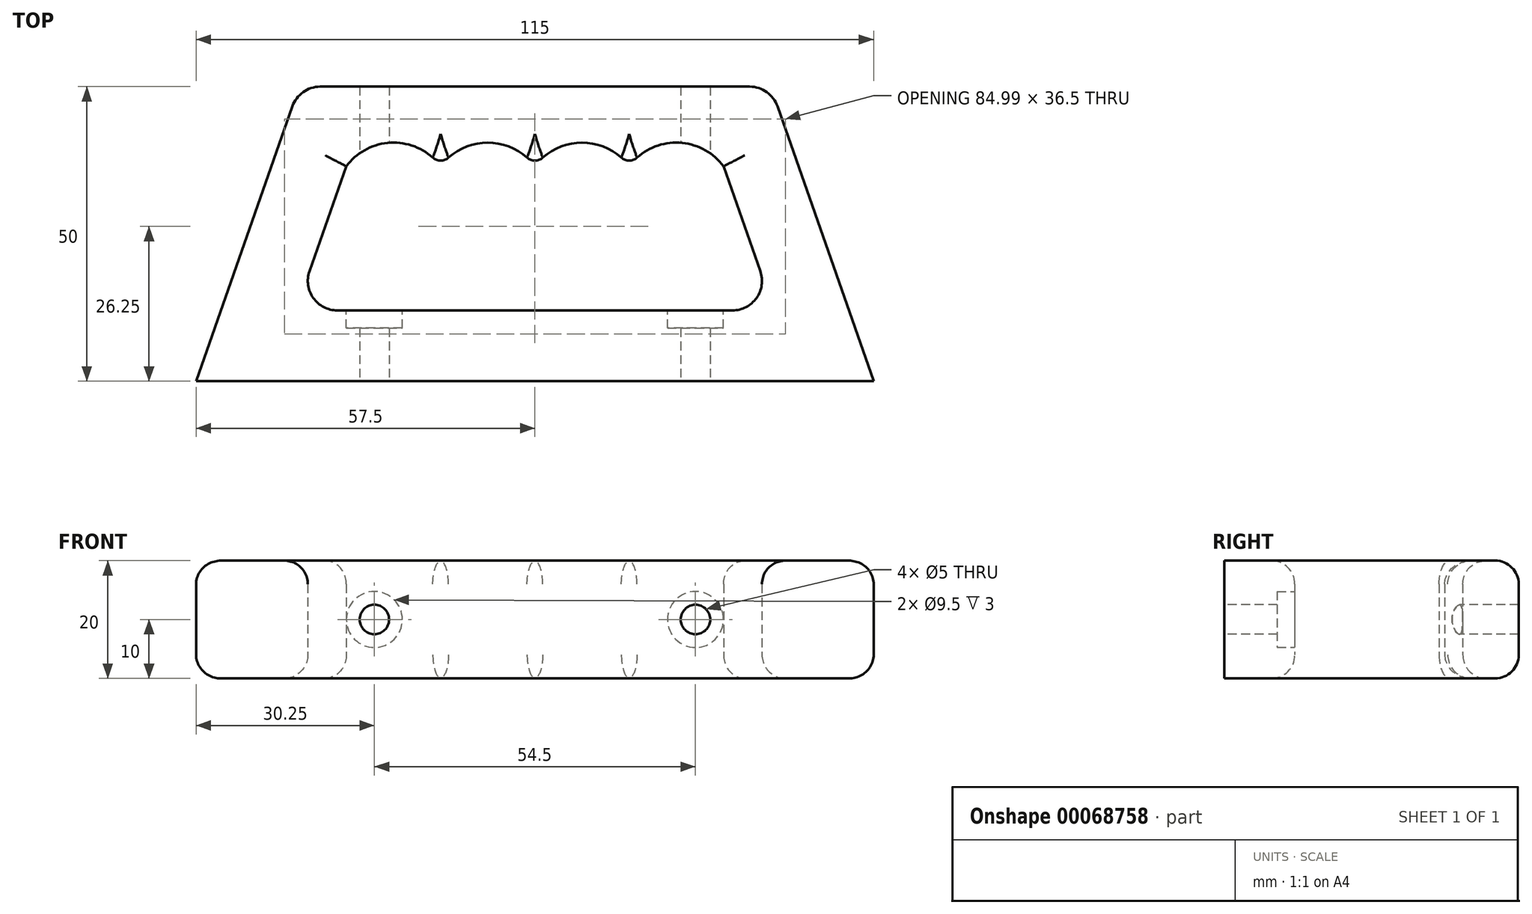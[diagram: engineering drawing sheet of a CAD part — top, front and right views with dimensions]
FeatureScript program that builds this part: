
annotation { "Feature Type Name" : "Feature", "Feature Type Description" : "" }
export const myFeature = defineFeature(function(context is Context, id is Id, definition is map)
    precondition{}
    {
        {
            var Q0;
            Q0=qCreatedBy(makeId("Top.planeOp"),FACE);
            var sketch = newSketch(context, id + "F0", { "sketchPlane" : qUnion([Q0])});
            skLineSegment(sketch, "E0.rect.bottom", {"start": v(57.5, 25) * mm, "end": v(-57.5, 25) * mm, "construction": true});
            skLineSegment(sketch, "E0.rect.top", {"start": v(57.5, -25) * mm, "end": v(-57.5, -25) * mm, "construction": true});
            skLineSegment(sketch, "E0.rect.left", {"start": v(57.5, 25) * mm, "end": v(57.5, -25) * mm, "construction": true});
            skLineSegment(sketch, "E0.rect.right", {"start": v(-57.5, 25) * mm, "end": v(-57.5, -25) * mm, "construction": true});
            skPoint(sketch, "E0.rect.middle", {"position": v(0, 0) * mm});
            skLineSegment(sketch, "E1", {"start": v(-57.5, -25) * mm, "end": v(57.5, -25) * mm});
            skLineSegment(sketch, "E2", {"start": v(57.5, -25) * mm, "end": v(41.17, 21.65) * mm});
            skLineSegment(sketch, "E3", {"start": v(36.45, 25) * mm, "end": v(-36.45, 25) * mm});
            skLineSegment(sketch, "E4", {"start": v(-41.17, 21.65) * mm, "end": v(-57.5, -25) * mm});
            skLineSegment(sketch, "E5.rect.bottom", {"start": v(24, 5.5) * mm, "end": v(-24, 5.5) * mm, "construction": true});
            skLineSegment(sketch, "E5.rect.top", {"start": v(24, -5.5) * mm, "end": v(-24, -5.5) * mm, "construction": true});
            skLineSegment(sketch, "E5.rect.left", {"start": v(24, 5.5) * mm, "end": v(24, -5.5) * mm, "construction": true});
            skLineSegment(sketch, "E5.rect.right", {"start": v(-24, 5.5) * mm, "end": v(-24, -5.5) * mm, "construction": true});
            skPoint(sketch, "E6.visualSharp", {"position": v(-40, 25) * mm});
            skArc(sketch, "E6.filletArc", {"start": v(-36.45, 25) * mm, "mid": v(-39.35, 24.08) * mm, "end": v(-41.17, 21.65) * mm});
            skPoint(sketch, "E7.visualSharp", {"position": v(40, 25) * mm});
            skArc(sketch, "E7.filletArc", {"start": v(41.17, 21.65) * mm, "mid": v(39.35, 24.08) * mm, "end": v(36.45, 25) * mm});
            skLineSegment(sketch, "E8.0", {"start": v(-32.02, 11.47) * mm, "end": v(-38.26, -6.35) * mm});
            skLineSegment(sketch, "E8.2", {"start": v(38.26, -6.35) * mm, "end": v(32.02, 11.47) * mm});
            skLineSegment(sketch, "E8.3", {"start": v(-33.54, -13) * mm, "end": v(33.54, -13) * mm});
            skArc(sketch, "E9", {"start": v(-16, 11.5) * mm, "mid": v(-24.02, 15.5) * mm, "end": v(-32.02, 11.47) * mm});
            skArc(sketch, "E10.1.0.0", {"start": v(0, 11.5) * mm, "mid": v(-8, 15.5) * mm, "end": v(-16, 11.5) * mm});
            skArc(sketch, "E10.2.0.0", {"start": v(16, 11.5) * mm, "mid": v(8, 15.5) * mm, "end": v(0, 11.5) * mm});
            skArc(sketch, "E10.3.0.0", {"start": v(32.02, 11.47) * mm, "mid": v(24.02, 15.5) * mm, "end": v(16, 11.5) * mm});
            skLineSegment(sketch, "E10.direction1", {"start": v(-24, 5.5) * mm, "end": v(-8, 5.5) * mm, "construction": true});
            skPoint(sketch, "E11.orphan", {"position": v(31.49, 13) * mm});
            skPoint(sketch, "E12.visualSharp", {"position": v(-40.59, -13) * mm});
            skArc(sketch, "E12.filletArc", {"start": v(-38.26, -6.35) * mm, "mid": v(-37.62, -10.9) * mm, "end": v(-33.54, -13) * mm});
            skPoint(sketch, "E13.visualSharp", {"position": v(40.59, -13) * mm});
            skArc(sketch, "E13.filletArc", {"start": v(33.54, -13) * mm, "mid": v(37.62, -10.9) * mm, "end": v(38.26, -6.35) * mm});
            skSolve(sketch);
        }
        {
            var Q0;
            Q0=makeQuery(id+"F0.imprint","IMPRINT",FACE,{"disambiguationData":[TD([[makeQuery(id+"F0.imprint","IMPRINT",EDGE,{"derivedFrom":sQuery(id+"F0.wireOp",EDGE,"E1")}),1.0]])]});
            extrude(context, id + "F1", {"entities" : qUnion([Q0]), "depth" : 20 * mm});
        }
        {
            var Q0;
            Q0=makeQuery(id+"F1.opExtrude","CAP_EDGE",EDGE,{"disambiguationData":[OSD([sQuery(id+"F0.wireOp",EDGE,"E9")])],"isStart":false});
            var Q1;
            Q1=makeQuery(id+"F1.opExtrude","CAP_EDGE",EDGE,{"disambiguationData":[OSD([sQuery(id+"F0.wireOp",EDGE,"E10.1.0.0")])],"isStart":false});
            var Q2;
            Q2=makeQuery(id+"F1.opExtrude","CAP_EDGE",EDGE,{"disambiguationData":[OSD([sQuery(id+"F0.wireOp",EDGE,"E10.2.0.0")])],"isStart":false});
            var Q3;
            Q3=makeQuery(id+"F1.opExtrude","CAP_EDGE",EDGE,{"disambiguationData":[OSD([sQuery(id+"F0.wireOp",EDGE,"E10.3.0.0")])],"isStart":false});
            var Q4;
            Q4=makeQuery(id+"F1.opExtrude","CAP_EDGE",EDGE,{"disambiguationData":[OSD([sQuery(id+"F0.wireOp",EDGE,"E8.2")])],"isStart":false});
            var Q5;
            Q5=makeQuery(id+"F1.opExtrude","CAP_EDGE",EDGE,{"disambiguationData":[OSD([sQuery(id+"F0.wireOp",EDGE,"E3")])],"isStart":false});
            var Q6;
            Q6=makeQuery(id+"F1.opExtrude","CAP_EDGE",EDGE,{"disambiguationData":[OSD([sQuery(id+"F0.wireOp",EDGE,"E3")])],"isStart":true});
            var Q7;
            Q7=makeQuery(id+"F1.opExtrude","CAP_EDGE",EDGE,{"disambiguationData":[OSD([sQuery(id+"F0.wireOp",EDGE,"E10.3.0.0")])],"isStart":true});
            var Q8;
            Q8=makeQuery(id+"F1.opExtrude","CAP_EDGE",EDGE,{"disambiguationData":[OSD([sQuery(id+"F0.wireOp",EDGE,"E10.2.0.0")])],"isStart":true});
            var Q9;
            Q9=makeQuery(id+"F1.opExtrude","CAP_EDGE",EDGE,{"disambiguationData":[OSD([sQuery(id+"F0.wireOp",EDGE,"E10.1.0.0")])],"isStart":true});
            var Q10;
            Q10=makeQuery(id+"F1.opExtrude","CAP_EDGE",EDGE,{"disambiguationData":[OSD([sQuery(id+"F0.wireOp",EDGE,"E9")])],"isStart":true});
            var Q11;
            Q11=makeQuery(id+"F1.opExtrude","CAP_EDGE",EDGE,{"disambiguationData":[OSD([sQuery(id+"F0.wireOp",EDGE,"E8.0")])],"isStart":true});
            fillet(context, id + "F2", {"entities" : qUnion([Q0, Q1, Q2, Q3, Q4, Q5, Q6, Q7, Q8, Q9, Q10, Q11]), "radius" : 4 * mm, "tangentPropagation" : true, "allowEdgeOverflow" : false});
        }
        {
            var Q0;
            Q0=makeQuery(id+"F1.opExtrude","SWEPT_EDGE",EDGE,{"disambiguationData":[OSD([sQuery(id+"F0.wireOp",EDGE,"E9"),sQuery(id+"F0.wireOp",EDGE,"E10.1.0.0")])]});
            var Q1;
            Q1=makeQuery(id+"F1.opExtrude","SWEPT_EDGE",EDGE,{"disambiguationData":[OSD([sQuery(id+"F0.wireOp",EDGE,"E10.1.0.0"),sQuery(id+"F0.wireOp",EDGE,"E10.2.0.0")])]});
            var Q2;
            Q2=makeQuery(id+"F1.opExtrude","SWEPT_EDGE",EDGE,{"disambiguationData":[OSD([sQuery(id+"F0.wireOp",EDGE,"E10.2.0.0"),sQuery(id+"F0.wireOp",EDGE,"E10.3.0.0")])]});
            fillet(context, id + "F3", {"entities" : qUnion([Q0, Q1, Q2]), "radius" : 2 * mm, "tangentPropagation" : true, "allowEdgeOverflow" : false});
        }
        {
            var Q0;
            Q0=makeQuery(id+"F1.opExtrude","SWEPT_FACE",FACE,{"disambiguationData":[OSD([sQuery(id+"F0.wireOp",EDGE,"E1")])]});
            var sketch = newSketch(context, id + "F4", { "sketchPlane" : qUnion([Q0])});
            skLineSegment(sketch, "E14", {"start": v(0, 42.89) * mm, "end": v(0, -21.26) * mm, "construction": true});
            skPoint(sketch, "E14.endSnap0", {"position": v(0, 5) * mm});
            skLineSegment(sketch, "E15.rect.bottom", {"start": v(27.25, 26.8) * mm, "end": v(-27.25, 26.8) * mm, "construction": true});
            skLineSegment(sketch, "E15.rect.top", {"start": v(27.25, -5.17) * mm, "end": v(-27.25, -5.17) * mm, "construction": true});
            skLineSegment(sketch, "E15.rect.left", {"start": v(27.25, 26.8) * mm, "end": v(27.25, -5.17) * mm, "construction": true});
            skLineSegment(sketch, "E15.rect.right", {"start": v(-27.25, 26.8) * mm, "end": v(-27.25, -5.17) * mm, "construction": true});
            skPoint(sketch, "E15.rect.middle", {"position": v(0, 10.81) * mm});
            skLineSegment(sketch, "E16", {"start": v(-57.5, 10) * mm, "end": v(57.5, 10) * mm, "construction": true});
            skCircle(sketch, "E17", {"center": v(-27.25, 10) * mm, "radius": 2.5 * mm});
            skCircle(sketch, "E18", {"center": v(27.25, 10) * mm, "radius": 2.5 * mm});
            skSolve(sketch);
        }
        {
            var Q0;
            Q0=makeQuery(id+"F4.imprint","IMPRINT",FACE,{"disambiguationData":[TD([[makeQuery(id+"F4.imprint","IMPRINT",EDGE,{"derivedFrom":sQuery(id+"F4.wireOp",EDGE,"E17")}),1.0]])]});
            var Q1;
            Q1=makeQuery(id+"F4.imprint","IMPRINT",FACE,{"disambiguationData":[TD([[makeQuery(id+"F4.imprint","IMPRINT",EDGE,{"derivedFrom":sQuery(id+"F4.wireOp",EDGE,"E18")}),1.0]])]});
            extrude(context, id + "F5", {"entities" : qUnion([Q0, Q1]), "operationType" : NewBodyOperationType.REMOVE, "endBound" : BoundingType.THROUGH_ALL, "oppositeDirection" : true, "depth" : 25 * mm});
        }
        {
            var Q0;
            Q0=makeQuery(id+"F1.opExtrude","SWEPT_FACE",FACE,{"disambiguationData":[OSD([sQuery(id+"F0.wireOp",EDGE,"E8.3")])]});
            var sketch = newSketch(context, id + "F6", { "sketchPlane" : qUnion([Q0])});
            skCircle(sketch, "E19", {"center": v(27.25, 10) * mm, "radius": 4.75 * mm});
            skCircle(sketch, "E20", {"center": v(-27.25, 10) * mm, "radius": 4.75 * mm});
            skSolve(sketch);
        }
        {
            var Q0;
            Q0=makeQuery(id+"F6.imprint","IMPRINT",FACE,{"disambiguationData":[TD([[makeQuery(id+"F6.imprint","IMPRINT",EDGE,{"derivedFrom":sQuery(id+"F6.wireOp",EDGE,"E19")}),1.0]])]});
            var Q1;
            Q1=makeQuery(id+"F6.imprint","IMPRINT",FACE,{"disambiguationData":[TD([[makeQuery(id+"F6.imprint","IMPRINT",EDGE,{"derivedFrom":sQuery(id+"F6.wireOp",EDGE,"E20")}),1.0]])]});
            extrude(context, id + "F7", {"entities" : qUnion([Q0, Q1]), "operationType" : NewBodyOperationType.REMOVE, "oppositeDirection" : true, "depth" : 3 * mm});
        }
    });
